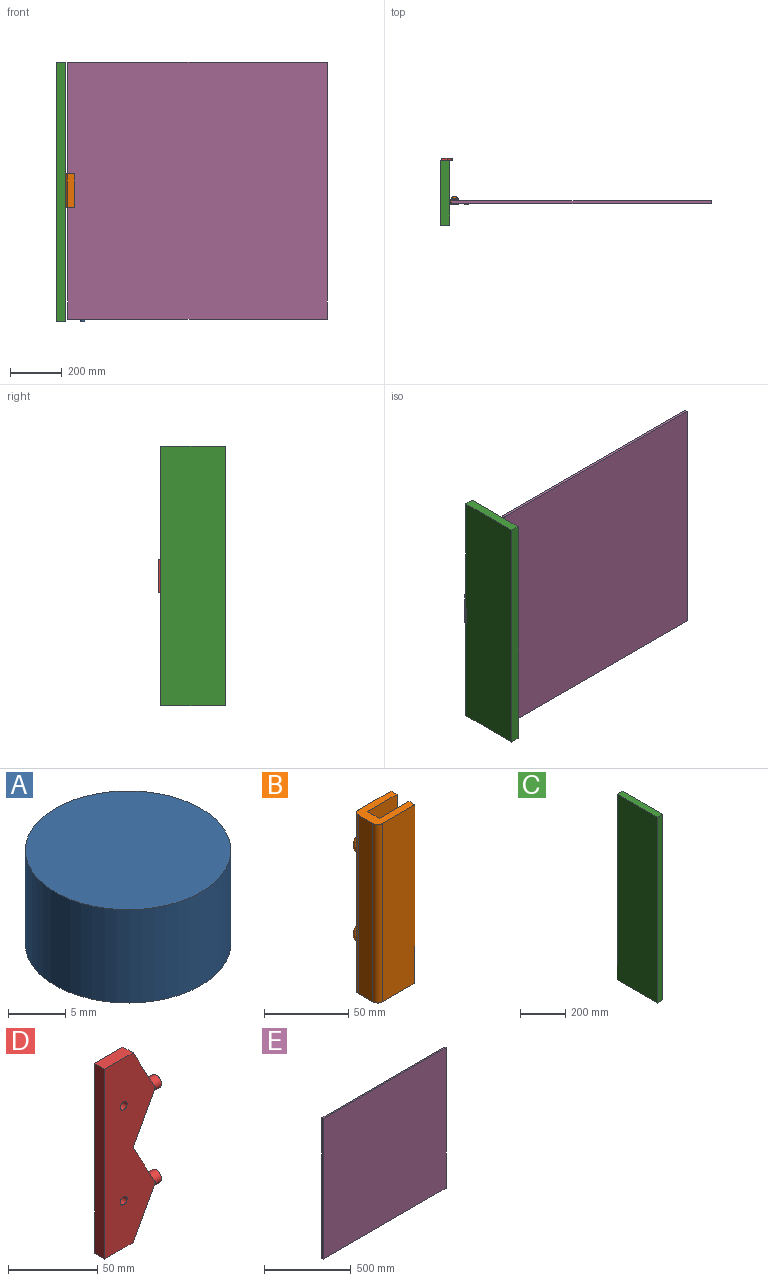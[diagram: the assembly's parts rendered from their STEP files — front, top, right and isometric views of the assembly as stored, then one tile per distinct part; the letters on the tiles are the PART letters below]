
ASSEMBLY  parts=5 mates=3
PART A: 3 faces, bbox 18x18x10 mm
  f0: cylinder r=9mm len=18mm, axis (0,0,-1), area 565.5mm2, adj f1,f2
  f1: plane 18x18mm, normal (0,0,1), area 254.5mm2, adj f0
  f2: plane 18x18mm, normal (0,0,-1), area 254.5mm2, adj f0
PART B: 22 faces, bbox 31.8x34.3x130.2 mm
  f0: plane 130x10mm, normal (1,0,0), area 1300mm2, adj f1,f3,f6,f8
  f1: plane 31.4x20mm, normal (0,0,1), area 371.1mm2, adj f0,f2,f4,f5,f6,f7,f8,f9
  f2: plane 130x27.4mm, normal (0,1,0), area 3337.6mm2, adj f1,f3,f7,f11,f18,f20
  f3: plane 31.4x20mm, normal (0,0,-1), area 371.1mm2, adj f0,f2,f4,f5,f6,f7,f8,f9
  f4: plane 130x27.4mm, normal (0,-1,0), area 3562mm2, adj f1,f3,f9,f10
  f5: plane 130x12mm, normal (-1,0,0), area 1560mm2, adj f1,f3,f10,f11
  f6: plane 130x25mm, normal (0,-1,0), area 3250mm2, adj f0,f1,f3,f7
  f7: plane 130.19x5.19mm, normal (1,0,0), area 650mm2, adj f1,f2,f3,f6,f19,f21
  f8: plane 130x25mm, normal (0,1,0), area 3250mm2, adj f0,f1,f3,f9
  f9: plane 130x5mm, normal (1,0,0), area 650mm2, adj f1,f3,f4,f8
  f10: cylinder r=4mm len=130mm, axis (0,0,-1), area 816.8mm2, adj f1,f3,f4,f5
  f11: cylinder r=4mm len=130mm, axis (0,0,1), area 816.8mm2, adj f1,f2,f3,f5
  f12: torus R=9mm, axis (0,0,-1), area 498.1mm2, adj f17,f18,f19
  f13: plane 2x2mm, normal (-0.34,-0.94,0), area 3.3mm2, adj f17
  f14: torus R=9mm, axis (0,0,-1), area 498.1mm2, adj f16,f20,f21
  f15: plane 2x2mm, normal (-0.34,-0.94,0), area 3.3mm2, adj f16
  f16: bspline ~9.1x8.29mm, area 85.6mm2, adj f14,f15
  f17: bspline ~9.1x8.29mm, area 85.6mm2, adj f12,f13
  f18: bspline ~12x11.45mm, area 84.9mm2, adj f2,f12,f19
  f19: bspline ~7.85x2.02mm, area 11.7mm2, adj f7,f12,f18
  f20: bspline ~12x11.45mm, area 84.9mm2, adj f2,f14,f21
  f21: bspline ~7.85x2.02mm, area 11.7mm2, adj f7,f14,f20
PART C: 6 faces, bbox 35x250x1000 mm
  f0: plane 1000x250mm, normal (1,0,0), area 250000mm2, adj f1,f3,f4,f5
  f1: plane 1000x35mm, normal (0,1,0), area 35000mm2, adj f0,f2,f4,f5
  f2: plane 1000x250mm, normal (-1,0,0), area 250000mm2, adj f1,f3,f4,f5
  f3: plane 1000x35mm, normal (0,-1,0), area 35000mm2, adj f0,f2,f4,f5
  f4: plane 250x35mm, normal (0,0,1), area 8750mm2, adj f0,f1,f2,f3
  f5: plane 250x35mm, normal (0,0,-1), area 8750mm2, adj f0,f1,f2,f3
PART D: 23 faces, bbox 45x8x130 mm
  f0: cylinder r=4mm len=8mm, axis (-1,0,0), area 150.3mm2, adj f5,f10,f11,f20,f21,f22
  f1: cylinder r=4mm len=8mm, axis (-1,0,0), area 150.3mm2, adj f4,f9,f12,f17,f18,f19
  f2: plane 130x39.19mm, normal (0,1,0), area 3863.7mm2, adj f6,f7,f8,f9,f10,f11,f12,f15
  f3: plane 130x40.19mm, normal (0,-1,0), area 4027.6mm2, adj f6,f7,f8,f9,f10,f11,f12,f13
  f4: plane 8x8mm, normal (1,0,0), area 50.3mm2, adj f1
  f5: plane 8x8mm, normal (1,0,0), area 50.3mm2, adj f0
  f6: plane 22.5x8mm, normal (0,0,-1), area 180mm2, adj f2,f3,f7,f12
  f7: plane 130x8mm, normal (-1,0,0), area 1040mm2, adj f2,f3,f6,f8
  f8: plane 22.5x8mm, normal (0,0,1), area 180mm2, adj f2,f3,f7,f11
  f9: plane 32.5x17.69mm, normal (0.88,0,0.48), area 267.1mm2, adj f1,f2,f3,f10,f18
  f10: plane 32.5x17.69mm, normal (0.88,0,-0.48), area 267.1mm2, adj f0,f2,f3,f9,f21
  f11: plane 32.5x17.69mm, normal (0.88,0,0.48), area 267.1mm2, adj f0,f2,f3,f8,f21
  f12: plane 32.5x17.69mm, normal (0.88,0,-0.48), area 267.1mm2, adj f1,f2,f3,f6,f18
  f13: cylinder r=2.75mm len=5.5mm, axis (0,1,0), area 86.4mm2, adj f3,f16
  f14: cylinder r=2.75mm len=5.5mm, axis (0,1,0), area 86.4mm2, adj f3,f15
  f15: cone r=5.75mm half-angle=45deg, axis (0,1,0), area 113.3mm2, adj f2,f14
  f16: cone r=2.75mm half-angle=45deg, axis (0,1,0), area 113.3mm2, adj f2,f13
  f17: plane 6.25x1mm, normal (0,1,0), area 6.2mm2, adj f1,f18,f19
  f18: plane 6.25x1.5mm, normal (1,0,0), area 7.1mm2, adj f1,f2,f9,f12,f17
  f19: plane 6.25x1.5mm, normal (-1,0,0), area 6.5mm2, adj f1,f17
  f20: plane 6.25x1.5mm, normal (-1,0,0), area 6.5mm2, adj f0,f22
  f21: plane 6.25x1.5mm, normal (1,0,0), area 7.1mm2, adj f0,f2,f10,f11,f22
  f22: plane 6.25x1mm, normal (0,1,0), area 6.2mm2, adj f0,f20,f21
PART E: 6 faces, bbox 1000x10x990 mm
  f0: plane 1000x990mm, normal (0,-1,0), area 990000mm2, adj f1,f3,f4,f5
  f1: plane 990x10mm, normal (1,0,0), area 9900mm2, adj f0,f2,f4,f5
  f2: plane 1000x990mm, normal (0,1,0), area 990000mm2, adj f1,f3,f4,f5
  f3: plane 990x10mm, normal (-1,0,0), area 9900mm2, adj f0,f2,f4,f5
  f4: plane 1000x10mm, normal (0,0,1), area 10000mm2, adj f0,f1,f2,f3
  f5: plane 1000x10mm, normal (0,0,-1), area 10000mm2, adj f0,f1,f2,f3
PLACE A t=(3,0,0)mm fixed
PLACE B t=(0,0,228.13)mm
PLACE C at identity fixed
PLACE D t=(1.4,0,223.68)mm
PLACE E at identity
MATE fastened C.f1 <-> D.f3  axis (0,1,0) through (-25,156,500)mm
MATE revolute A.f0 <-> E.f5  axis (0,0,1) through (56,-5,10)mm
MATE fastened E.f3 <-> B.f0  axis (-1,0,0) through (0,-5,505)mm
